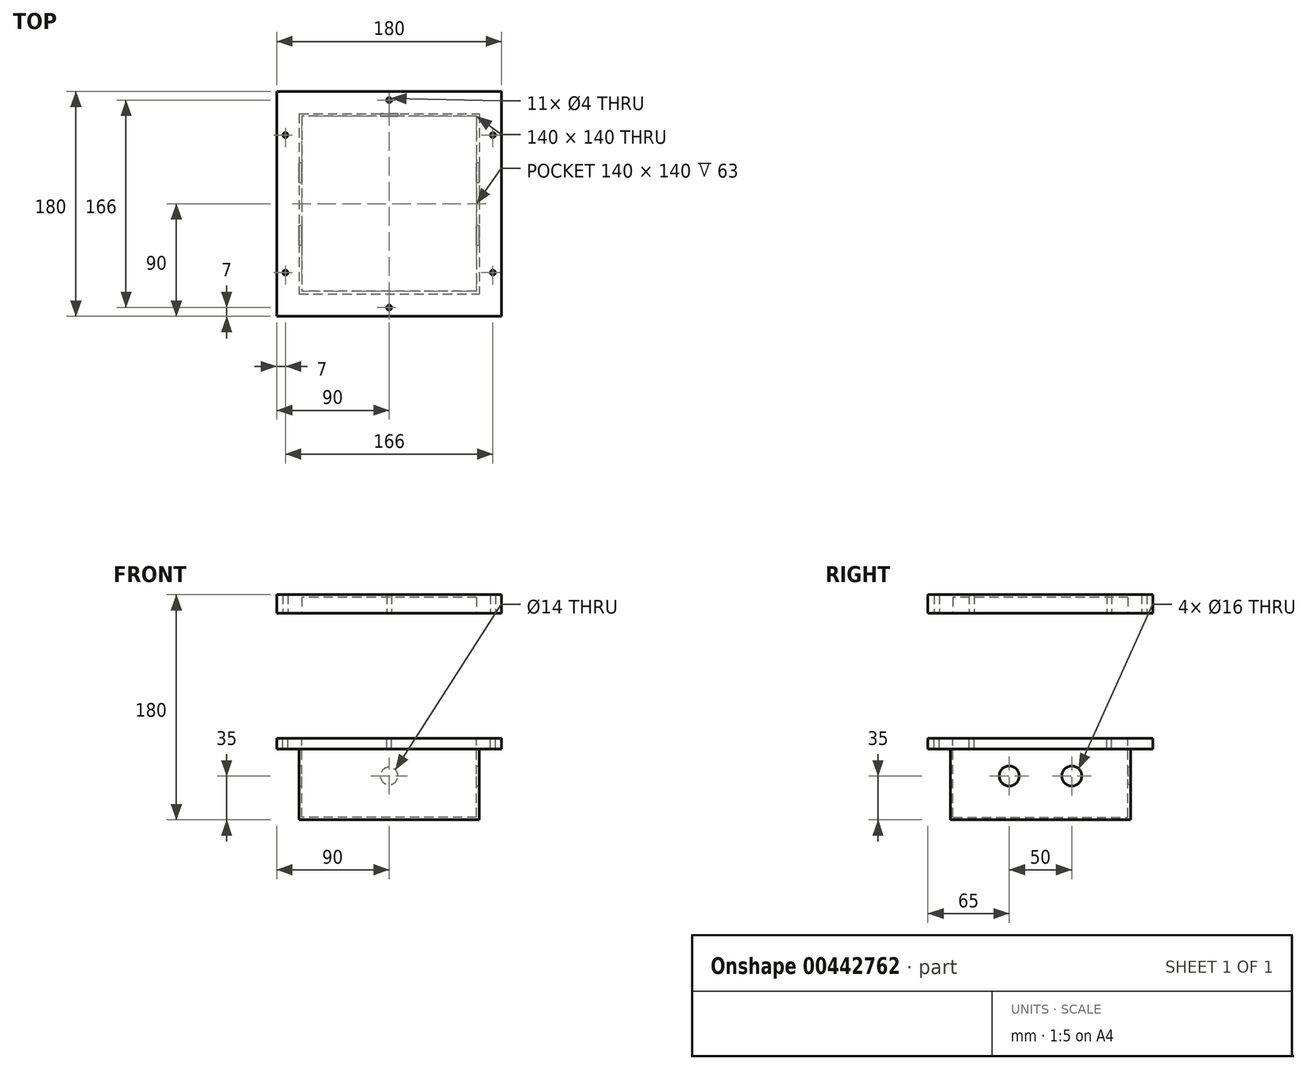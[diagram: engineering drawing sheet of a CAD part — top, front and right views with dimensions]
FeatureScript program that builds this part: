
annotation { "Feature Type Name" : "Feature", "Feature Type Description" : "" }
export const myFeature = defineFeature(function(context is Context, id is Id, definition is map)
    precondition{}
    {
        {
            var Q0;
            Q0=qCreatedBy(makeId("Top.planeOp"),FACE);
            var sketch = newSketch(context, id + "F0", { "sketchPlane" : qUnion([Q0])});
            skLineSegment(sketch, "E0.bottom", {"start": v(72, -72) * mm, "end": v(-72, -72) * mm});
            skLineSegment(sketch, "E0.top", {"start": v(72, 72) * mm, "end": v(-72, 72) * mm});
            skLineSegment(sketch, "E0.left", {"start": v(72, -72) * mm, "end": v(72, 72) * mm});
            skLineSegment(sketch, "E0.right", {"start": v(-72, -72) * mm, "end": v(-72, 72) * mm});
            skPoint(sketch, "E0.middle", {"position": v(0, 0) * mm});
            skSolve(sketch);
        }
        {
            var Q0;
            Q0 = qSketchRegion(id + "F0", true);
            extrude(context, id + "F1", {"entities" : qUnion([Q0]), "oppositeDirection" : true, "depth" : 65 * mm});
        }
        {
            var Q0;
            Q0=makeQuery(id+"F1.opExtrude","CAP_FACE",FACE,{"disambiguationData":[OSD([sQuery(id+"F0.wireOp",EDGE,"E0.bottom"),sQuery(id+"F0.wireOp",EDGE,"E0.top"),sQuery(id+"F0.wireOp",EDGE,"E0.left"),sQuery(id+"F0.wireOp",EDGE,"E0.right")])],"isStart":true});
            shell(context, id + "F2", {"entities" : qUnion([Q0]), "thickness" : 2 * mm});
        }
        {
            var Q0;
            Q0=qCreatedBy(makeId("Top.planeOp"),FACE);
            var sketch = newSketch(context, id + "F3", { "sketchPlane" : qUnion([Q0])});
            skLineSegment(sketch, "E1.bottom", {"start": v(90, 90) * mm, "end": v(-90, 90) * mm});
            skLineSegment(sketch, "E1.top", {"start": v(90, -90) * mm, "end": v(-90, -90) * mm});
            skLineSegment(sketch, "E1.left", {"start": v(90, 90) * mm, "end": v(90, -90) * mm});
            skLineSegment(sketch, "E1.right", {"start": v(-90, 90) * mm, "end": v(-90, -90) * mm});
            skPoint(sketch, "E1.middle", {"position": v(0, 0) * mm});
            skSolve(sketch);
        }
        {
            var Q0;
            Q0 = qSketchRegion(id + "F3", true);
            extrude(context, id + "F4", {"entities" : qUnion([Q0]), "operationType" : NewBodyOperationType.ADD, "oppositeDirection" : true, "depth" : 8.5 * mm});
        }
        {
            var Q0;
            Q0=qCreatedBy(makeId("Top.planeOp"),FACE);
            var sketch = newSketch(context, id + "F5", { "sketchPlane" : qUnion([Q0])});
            skLineSegment(sketch, "E2.bottom", {"start": v(70, 70) * mm, "end": v(-70, 70) * mm});
            skLineSegment(sketch, "E2.top", {"start": v(70, -70) * mm, "end": v(-70, -70) * mm});
            skLineSegment(sketch, "E2.left", {"start": v(70, 70) * mm, "end": v(70, -70) * mm});
            skLineSegment(sketch, "E2.right", {"start": v(-70, 70) * mm, "end": v(-70, -70) * mm});
            skPoint(sketch, "E2.middle", {"position": v(0, 0) * mm});
            skSolve(sketch);
        }
        {
            var Q0;
            Q0 = qSketchRegion(id + "F5", true);
            extrude(context, id + "F6", {"entities" : qUnion([Q0]), "operationType" : NewBodyOperationType.REMOVE, "oppositeDirection" : true, "depth" : 10 * mm});
        }
        {
            var Q0;
            Q0=qCreatedBy(makeId("Top.planeOp"),FACE);
            var sketch = newSketch(context, id + "F7", { "sketchPlane" : qUnion([Q0])});
            skCircle(sketch, "E3", {"center": v(-83, 55) * mm, "radius": 2 * mm});
            skCircle(sketch, "E4.MirrorC", {"center": v(-83, -55) * mm, "radius": 2 * mm});
            skCircle(sketch, "E5.MirrorC", {"center": v(83, 55) * mm, "radius": 2 * mm});
            skCircle(sketch, "E6.MirrorC", {"center": v(83, -55) * mm, "radius": 2 * mm});
            skSolve(sketch);
        }
        {
            var Q0;
            Q0 = qSketchRegion(id + "F7", true);
            var Q1;
            {var subQ0=sQuery(id+"F3.wireOp",EDGE,"E1.bottom");var subQ1=sQuery(id+"F3.wireOp",EDGE,"E1.top");var subQ2=sQuery(id+"F3.wireOp",EDGE,"E1.left");var subQ3=sQuery(id+"F3.wireOp",EDGE,"E1.right");Q1=makeQuery(id+"F4.boolean.opBoolean","SPLIT",FACE,{"disambiguationData":[TD([makeQuery(id+"F1.opExtrude","SWEPT_FACE",FACE,{"disambiguationData":[OSD([sQuery(id+"F0.wireOp",EDGE,"E0.bottom")])]})])],"derivedFrom":makeQuery(id+"F4.opExtrude","CAP_FACE",FACE,{"disambiguationData":[OSD([subQ0,subQ1,subQ2,subQ3])],"isStart":false})});}
            var Q2;
            Q2=makeQuery(id+"F13.opExtrude","CAP_FACE",FACE,{"disambiguationData":[OSD([sQuery(id+"F12.wireOp",EDGE,"E9.bottom"),sQuery(id+"F12.wireOp",EDGE,"E9.top"),sQuery(id+"F12.wireOp",EDGE,"E9.left"),sQuery(id+"F12.wireOp",EDGE,"E9.right")])],"isStart":false});
            extrude(context, id + "F8", {"entities" : qUnion([Q0]), "operationType" : NewBodyOperationType.REMOVE, "endBound" : BoundingType.UP_TO_SURFACE, "oppositeDirection" : true, "endBoundEntityFace" : qUnion([Q1]), "depth" : 25 * mm, "hasSecondDirection" : true, "secondDirectionOppositeDirection" : false, "secondDirectionBoundEntityFace" : qUnion([Q2]), "secondDirectionDepth" : 150 * mm});
        }
        {
            var Q0;
            Q0=qCreatedBy(makeId("Top.planeOp"),FACE);
            var sketch = newSketch(context, id + "F9", { "sketchPlane" : qUnion([Q0])});
            skCircle(sketch, "E7", {"center": v(0, -83) * mm, "radius": 2 * mm});
            skCircle(sketch, "E8.MirrorC", {"center": v(0, 83) * mm, "radius": 2 * mm});
            skSolve(sketch);
        }
        {
            var Q0;
            Q0=makeQuery(id+"F9.imprint","IMPRINT",FACE,{"disambiguationData":[TD([[makeQuery(id+"F9.imprint","IMPRINT",EDGE,{"derivedFrom":sQuery(id+"F9.wireOp",EDGE,"E8.MirrorC")}),-1.0]])]});
            var Q1;
            Q1=makeQuery(id+"F9.imprint","IMPRINT",FACE,{"disambiguationData":[TD([[makeQuery(id+"F9.imprint","IMPRINT",EDGE,{"derivedFrom":sQuery(id+"F9.wireOp",EDGE,"E7")}),1.0]])]});
            var Q2;
            {var subQ0=sQuery(id+"F3.wireOp",EDGE,"E1.bottom");var subQ1=sQuery(id+"F3.wireOp",EDGE,"E1.top");var subQ2=sQuery(id+"F3.wireOp",EDGE,"E1.left");var subQ3=sQuery(id+"F3.wireOp",EDGE,"E1.right");Q2=makeQuery(id+"F4.boolean.opBoolean","SPLIT",FACE,{"disambiguationData":[TD([makeQuery(id+"F1.opExtrude","SWEPT_FACE",FACE,{"disambiguationData":[OSD([sQuery(id+"F0.wireOp",EDGE,"E0.bottom")])]})])],"derivedFrom":makeQuery(id+"F4.opExtrude","CAP_FACE",FACE,{"disambiguationData":[OSD([subQ0,subQ1,subQ2,subQ3])],"isStart":false})});}
            extrude(context, id + "F10", {"entities" : qUnion([Q0, Q1]), "operationType" : NewBodyOperationType.REMOVE, "endBound" : BoundingType.UP_TO_SURFACE, "oppositeDirection" : true, "endBoundEntityFace" : qUnion([Q2]), "depth" : 25 * mm, "hasSecondDirection" : true, "secondDirectionOppositeDirection" : false, "secondDirectionDepth" : 150 * mm});
        }
        {
            var Q0;
            Q0=qCreatedBy(makeId("Top.planeOp"),FACE);
            cPlane(context, id + "F11", {"entities" : qUnion([Q0]), "cplaneType" : CPlaneType.OFFSET, "offset" : 100 * mm, "width" : 150 * mm, "height" : 150 * mm});
        }
        {
            var Q0;
            Q0=qCreatedBy(id+"F11.planeOp",FACE);
            var sketch = newSketch(context, id + "F12", { "sketchPlane" : qUnion([Q0])});
            skLineSegment(sketch, "E9.bottom", {"start": v(-90, -90) * mm, "end": v(90, -90) * mm});
            skLineSegment(sketch, "E9.top", {"start": v(-90, 90) * mm, "end": v(90, 90) * mm});
            skLineSegment(sketch, "E9.left", {"start": v(-90, -90) * mm, "end": v(-90, 90) * mm});
            skLineSegment(sketch, "E9.right", {"start": v(90, -90) * mm, "end": v(90, 90) * mm});
            skSolve(sketch);
        }
        {
            var Q0;
            Q0 = qSketchRegion(id + "F12", true);
            extrude(context, id + "F13", {"entities" : qUnion([Q0]), "depth" : 15 * mm});
        }
        {
            var Q0;
            Q0=qCreatedBy(id+"F11.planeOp",FACE);
            var sketch = newSketch(context, id + "F14", { "sketchPlane" : qUnion([Q0])});
            skLineSegment(sketch, "E10.0", {"start": v(-70, 70) * mm, "end": v(-70, -70) * mm});
            skLineSegment(sketch, "E11.0", {"start": v(70, -70) * mm, "end": v(-70, -70) * mm});
            skLineSegment(sketch, "E12.0", {"start": v(70, 70) * mm, "end": v(70, -70) * mm});
            skLineSegment(sketch, "E13.0", {"start": v(70, 70) * mm, "end": v(-70, 70) * mm});
            skSolve(sketch);
        }
        {
            var Q0;
            Q0 = qSketchRegion(id + "F14", true);
            extrude(context, id + "F15", {"entities" : qUnion([Q0]), "operationType" : NewBodyOperationType.REMOVE, "depth" : 13 * mm});
        }
        {
            var Q0;
            Q0=qCreatedBy(id+"F11.planeOp",FACE);
            var sketch = newSketch(context, id + "F16", { "sketchPlane" : qUnion([Q0])});
            skCircle(sketch, "E14.0", {"center": v(-83, 55) * mm, "radius": 2 * mm});
            skCircle(sketch, "E15.0", {"center": v(-83, -55) * mm, "radius": 2 * mm});
            skCircle(sketch, "E16.0", {"center": v(0, -83) * mm, "radius": 2 * mm});
            skCircle(sketch, "E17.0", {"center": v(83, -55) * mm, "radius": 2 * mm});
            skCircle(sketch, "E18.0", {"center": v(0, 83) * mm, "radius": 2 * mm});
            skCircle(sketch, "E19.0", {"center": v(83, 55) * mm, "radius": 2 * mm});
            skSolve(sketch);
        }
        {
            var Q0;
            Q0 = qSketchRegion(id + "F16", true);
            var Q1;
            Q1=makeQuery(id+"F13.opExtrude","CAP_FACE",FACE,{"disambiguationData":[OSD([sQuery(id+"F12.wireOp",EDGE,"E9.bottom"),sQuery(id+"F12.wireOp",EDGE,"E9.top"),sQuery(id+"F12.wireOp",EDGE,"E9.left"),sQuery(id+"F12.wireOp",EDGE,"E9.right")])],"isStart":false});
            extrude(context, id + "F17", {"entities" : qUnion([Q0]), "operationType" : NewBodyOperationType.REMOVE, "endBound" : BoundingType.UP_TO_SURFACE, "endBoundEntityFace" : qUnion([Q1]), "depth" : 25 * mm});
        }
        {
            var Q0;
            Q0=qCreatedBy(makeId("Right.planeOp"),FACE);
            var sketch = newSketch(context, id + "F18", { "sketchPlane" : qUnion([Q0])});
            skCircle(sketch, "E20", {"center": v(-25, -30) * mm, "radius": 8 * mm});
            skCircle(sketch, "E21.MirrorC", {"center": v(25, -30) * mm, "radius": 8 * mm});
            skSolve(sketch);
        }
        {
            var Q0;
            Q0 = qSketchRegion(id + "F18", true);
            extrude(context, id + "F19", {"entities" : qUnion([Q0]), "operationType" : NewBodyOperationType.REMOVE, "oppositeDirection" : true, "depth" : 100 * mm, "hasSecondDirection" : true, "secondDirectionOppositeDirection" : false, "secondDirectionDepth" : 100 * mm});
        }
        {
            var Q0;
            Q0=qCreatedBy(makeId("Front.planeOp"),FACE);
            var sketch = newSketch(context, id + "F20", { "sketchPlane" : qUnion([Q0])});
            skCircle(sketch, "E22", {"center": v(0, -30) * mm, "radius": 7 * mm});
            skSolve(sketch);
        }
        {
            var Q0;
            Q0 = qSketchRegion(id + "F20", true);
            extrude(context, id + "F21", {"entities" : qUnion([Q0]), "operationType" : NewBodyOperationType.REMOVE, "oppositeDirection" : true, "depth" : 100 * mm});
        }
    });
